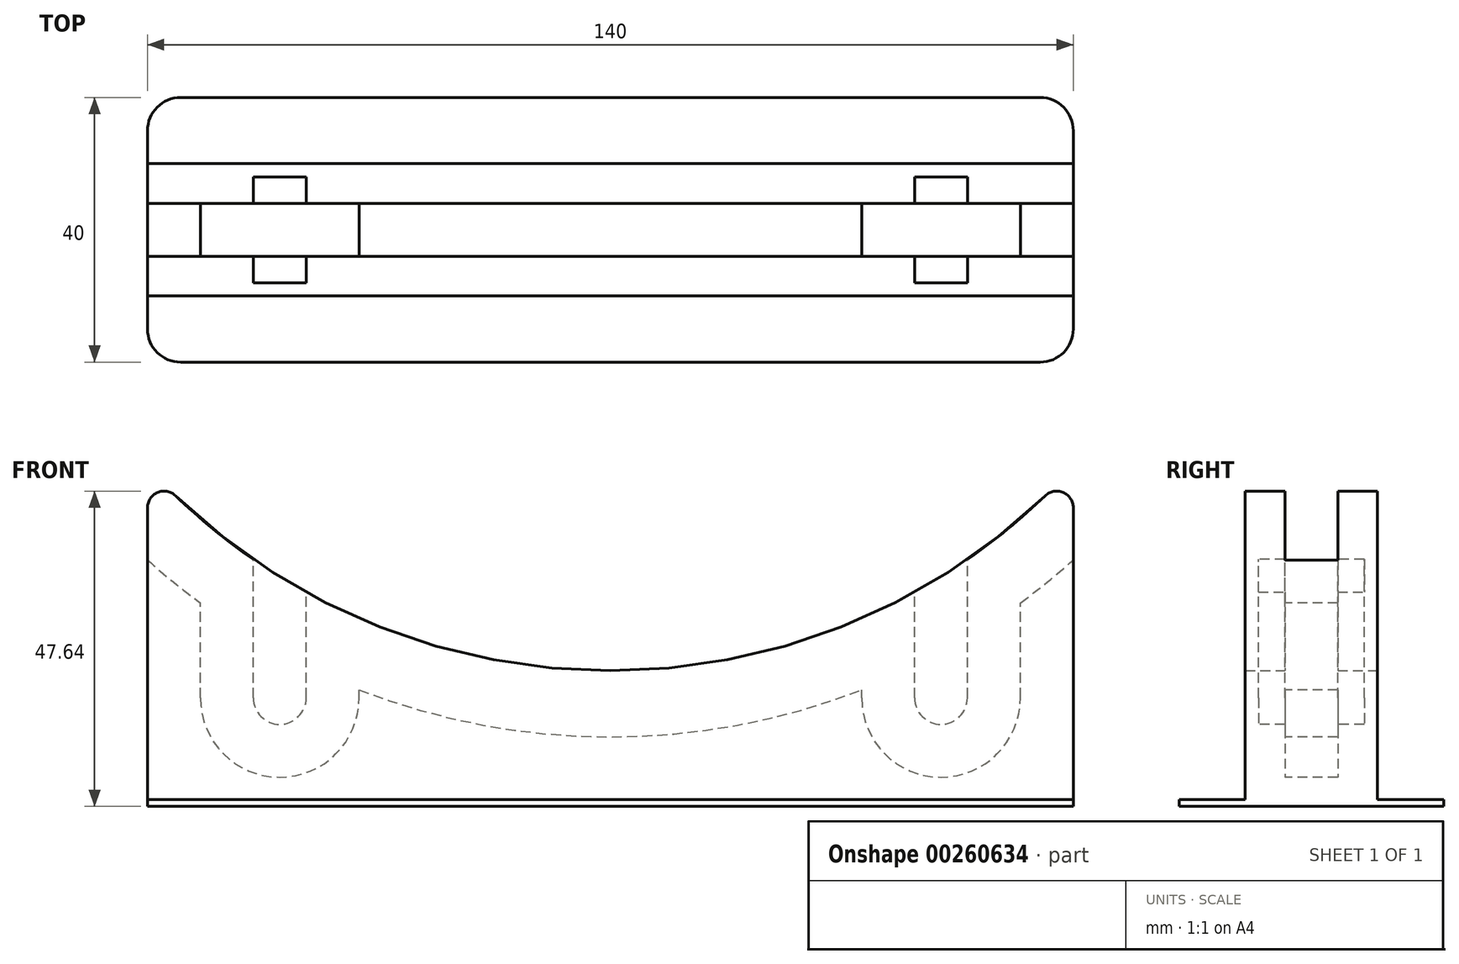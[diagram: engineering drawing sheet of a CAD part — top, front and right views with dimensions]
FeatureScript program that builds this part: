
annotation { "Feature Type Name" : "Feature", "Feature Type Description" : "" }
export const myFeature = defineFeature(function(context is Context, id is Id, definition is map)
    precondition{}
    {
        {
            var Q0;
            Q0=qCreatedBy(makeId("Front.planeOp"),FACE);
            var sketch = newSketch(context, id + "F0", { "sketchPlane" : qUnion([Q0])});
            skCircle(sketch, "E0", {"center": v(0, 115) * mm, "radius": 100 * mm, "construction": true});
            skLineSegment(sketch, "E1.top", {"start": v(-70, 0) * mm, "end": v(70, 0) * mm});
            skLineSegment(sketch, "E1.left", {"start": v(-70, 50.77) * mm, "end": v(-70, 0) * mm});
            skLineSegment(sketch, "E1.right", {"start": v(70, 50.77) * mm, "end": v(70, 0) * mm});
            skPoint(sketch, "E1.middle", {"position": v(0, 25.39) * mm});
            skArc(sketch, "E2", {"start": v(-70, 50.77) * mm, "mid": v(0, 20) * mm, "end": v(70, 50.77) * mm});
            skCircle(sketch, "E3", {"center": v(-50, 15.9) * mm, "radius": 11 * mm, "construction": true});
            skSolve(sketch);
        }
        {
            var Q0;
            Q0=makeQuery(id+"F0.imprint","IMPRINT",FACE,{"disambiguationData":[TD([[makeQuery(id+"F0.imprint","IMPRINT",EDGE,{"derivedFrom":sQuery(id+"F0.wireOp",EDGE,"E1.top")}),1.0]])]});
            extrude(context, id + "F1", {"entities" : qUnion([Q0]), "endBound" : BoundingType.SYMMETRIC, "depth" : 20 * mm, "hasSecondDirection" : true, "secondDirectionOppositeDirection" : true, "secondDirectionDepth" : 7.5 * mm});
        }
        {
            var Q0;
            Q0=qCreatedBy(makeId("Front.planeOp"),FACE);
            var sketch = newSketch(context, id + "F2", { "sketchPlane" : qUnion([Q0])});
            skCircle(sketch, "E4", {"center": v(0, 115) * mm, "radius": 100 * mm, "construction": true});
            skCircle(sketch, "E5", {"center": v(0, 115) * mm, "radius": 105 * mm});
            skSolve(sketch);
        }
        {
            var Q0;
            Q0=makeQuery(id+"F2.imprint","IMPRINT",FACE,{"disambiguationData":[TD([[makeQuery(id+"F2.imprint","IMPRINT",EDGE,{"derivedFrom":sQuery(id+"F2.wireOp",EDGE,"E5")}),1.0]])]});
            extrude(context, id + "F3", {"entities" : qUnion([Q0]), "operationType" : NewBodyOperationType.REMOVE, "oppositeDirection" : true, "depth" : 4 * mm, "hasSecondDirection" : true, "secondDirectionOppositeDirection" : false, "secondDirectionDepth" : 4 * mm});
        }
        {
            var Q0;
            {var subQ0=sQuery(id+"F0.wireOp",EDGE,"E2");var subQ1=sQuery(id+"F0.wireOp",EDGE,"E1.left");Q0=makeQuery(id+"F3.boolean.opBoolean","SPLIT",EDGE,{"disambiguationData":[TD([makeQuery(id+"F3.opExtrude","CAP_FACE",FACE,{"disambiguationData":[OSD([sQuery(id+"F2.wireOp",EDGE,"E5")])],"isStart":false})])],"derivedFrom":makeQuery(id+"F1.opExtrude","SWEPT_EDGE",EDGE,{"disambiguationData":[OSD([subQ1,subQ0])]})});}
            var Q1;
            {var subQ0=sQuery(id+"F0.wireOp",EDGE,"E2");var subQ1=sQuery(id+"F0.wireOp",EDGE,"E1.left");Q1=makeQuery(id+"F3.boolean.opBoolean","SPLIT",EDGE,{"disambiguationData":[TD([makeQuery(id+"F3.opExtrude","CAP_FACE",FACE,{"disambiguationData":[OSD([sQuery(id+"F2.wireOp",EDGE,"E5")])],"isStart":true})])],"derivedFrom":makeQuery(id+"F1.opExtrude","SWEPT_EDGE",EDGE,{"disambiguationData":[OSD([subQ1,subQ0])]})});}
            var Q2;
            {var subQ0=sQuery(id+"F0.wireOp",EDGE,"E2");var subQ1=sQuery(id+"F0.wireOp",EDGE,"E1.right");Q2=makeQuery(id+"F3.boolean.opBoolean","SPLIT",EDGE,{"disambiguationData":[TD([makeQuery(id+"F3.opExtrude","CAP_FACE",FACE,{"disambiguationData":[OSD([sQuery(id+"F2.wireOp",EDGE,"E5")])],"isStart":false})])],"derivedFrom":makeQuery(id+"F1.opExtrude","SWEPT_EDGE",EDGE,{"disambiguationData":[OSD([subQ1,subQ0])]})});}
            var Q3;
            {var subQ0=sQuery(id+"F0.wireOp",EDGE,"E2");var subQ1=sQuery(id+"F0.wireOp",EDGE,"E1.right");Q3=makeQuery(id+"F3.boolean.opBoolean","SPLIT",EDGE,{"disambiguationData":[TD([makeQuery(id+"F3.opExtrude","CAP_FACE",FACE,{"disambiguationData":[OSD([sQuery(id+"F2.wireOp",EDGE,"E5")])],"isStart":true})])],"derivedFrom":makeQuery(id+"F1.opExtrude","SWEPT_EDGE",EDGE,{"disambiguationData":[OSD([subQ1,subQ0])]})});}
            fillet(context, id + "F4", {"entities" : qUnion([Q0, Q1, Q2, Q3]), "radius" : 2.5 * mm, "tangentPropagation" : true, "allowEdgeOverflow" : false});
        }
        {
            var Q0;
            Q0=qCreatedBy(makeId("Front.planeOp"),FACE);
            var sketch = newSketch(context, id + "F5", { "sketchPlane" : qUnion([Q0])});
            skArc(sketch, "E6", {"start": v(-62, 15.9) * mm, "mid": v(-50, 3.9) * mm, "end": v(-38, 15.9) * mm});
            skCircle(sketch, "E7", {"center": v(0, 115) * mm, "radius": 100 * mm, "construction": true});
            skCircle(sketch, "E8", {"center": v(-50, 15.9) * mm, "radius": 11 * mm, "construction": true});
            skLineSegment(sketch, "E9.bottom", {"start": v(-62, 15.9) * mm, "end": v(-61, 15.9) * mm});
            skLineSegment(sketch, "E9.top", {"start": v(-62, 43.02) * mm, "end": v(-38, 43.02) * mm});
            skLineSegment(sketch, "E9.left", {"start": v(-62, 15.9) * mm, "end": v(-62, 43.02) * mm});
            skLineSegment(sketch, "E9.right", {"start": v(-38, 15.9) * mm, "end": v(-38, 43.02) * mm});
            skPoint(sketch, "E9.middle", {"position": v(-50, 29.46) * mm});
            skLineSegment(sketch, "E10.trimOffspring", {"start": v(-39, 15.9) * mm, "end": v(-38, 15.9) * mm});
            skLineSegment(sketch, "E11.MirrorCS", {"start": v(39, 15.9) * mm, "end": v(38, 15.9) * mm});
            skLineSegment(sketch, "E12.MirrorCS", {"start": v(62, 15.9) * mm, "end": v(61, 15.9) * mm});
            skArc(sketch, "E13.MirrorCS", {"start": v(62, 15.9) * mm, "mid": v(50, 3.9) * mm, "end": v(38, 15.9) * mm});
            skPoint(sketch, "E14.MirrorP", {"position": v(50, 29.46) * mm});
            skLineSegment(sketch, "E15.MirrorCS", {"start": v(38, 15.9) * mm, "end": v(38, 43.02) * mm});
            skLineSegment(sketch, "E16.MirrorCS", {"start": v(62, 43.02) * mm, "end": v(38, 43.02) * mm});
            skLineSegment(sketch, "E17.MirrorCS", {"start": v(62, 15.9) * mm, "end": v(62, 43.02) * mm});
            skCircle(sketch, "E18.MirrorC", {"center": v(50, 15.9) * mm, "radius": 11 * mm, "construction": true});
            skSolve(sketch);
        }
        {
            var Q0;
            Q0 = qSketchRegion(id + "F5", true);
            extrude(context, id + "F6", {"entities" : qUnion([Q0]), "operationType" : NewBodyOperationType.REMOVE, "endBound" : BoundingType.SYMMETRIC, "oppositeDirection" : true, "depth" : 8 * mm});
        }
        {
            var Q0;
            Q0=makeQuery(id+"F1.opExtrude","CAP_FACE",FACE,{"disambiguationData":[OSD([sQuery(id+"F0.wireOp",EDGE,"E1.top"),sQuery(id+"F0.wireOp",EDGE,"E1.left"),sQuery(id+"F0.wireOp",EDGE,"E1.right"),sQuery(id+"F0.wireOp",EDGE,"E2")])],"isStart":false});
            var sketch = newSketch(context, id + "F7", { "sketchPlane" : qUnion([Q0])});
            skArc(sketch, "E19", {"start": v(-54, 15.9) * mm, "mid": v(-50, 11.9) * mm, "end": v(-46, 15.9) * mm});
            skPoint(sketch, "E20.middle", {"position": v(-50, 26.4) * mm});
            skLineSegment(sketch, "E21", {"start": v(-54, 15.9) * mm, "end": v(-54, 36.84) * mm});
            skLineSegment(sketch, "E22", {"start": v(-54, 36.84) * mm, "end": v(-46, 36.84) * mm});
            skLineSegment(sketch, "E23", {"start": v(-46, 15.9) * mm, "end": v(-46, 36.84) * mm});
            skLineSegment(sketch, "E24.MirrorCS", {"start": v(54, 15.9) * mm, "end": v(54, 36.84) * mm});
            skLineSegment(sketch, "E25.MirrorCS", {"start": v(46, 15.9) * mm, "end": v(46, 36.84) * mm});
            skLineSegment(sketch, "E26.MirrorCS", {"start": v(54, 36.84) * mm, "end": v(46, 36.84) * mm});
            skPoint(sketch, "E27.MirrorP", {"position": v(50, 26.4) * mm});
            skArc(sketch, "E28.MirrorCS", {"start": v(54, 15.9) * mm, "mid": v(50, 11.9) * mm, "end": v(46, 15.9) * mm});
            skSolve(sketch);
        }
        {
            var Q0;
            Q0 = qSketchRegion(id + "F7", true);
            extrude(context, id + "F8", {"entities" : qUnion([Q0]), "operationType" : NewBodyOperationType.REMOVE, "oppositeDirection" : true, "depth" : 18 * mm, "hasSecondDirection" : true, "secondDirectionOppositeDirection" : true, "secondDirectionDepth" : 2 * mm});
        }
        {
            var Q0;
            Q0=qCreatedBy(makeId("Top.planeOp"),FACE);
            var sketch = newSketch(context, id + "F9", { "sketchPlane" : qUnion([Q0])});
            skLineSegment(sketch, "E29.bottom", {"start": v(-70, 20) * mm, "end": v(70, 20) * mm});
            skLineSegment(sketch, "E29.top", {"start": v(-70, -20) * mm, "end": v(70, -20) * mm});
            skLineSegment(sketch, "E29.left", {"start": v(-70, 20) * mm, "end": v(-70, -20) * mm});
            skLineSegment(sketch, "E29.right", {"start": v(70, 20) * mm, "end": v(70, -20) * mm});
            skPoint(sketch, "E29.middle", {"position": v(0, 0) * mm});
            skSolve(sketch);
        }
        {
            var Q0;
            Q0=makeQuery(id+"F9.imprint","IMPRINT",FACE,{"disambiguationData":[TD([[makeQuery(id+"F9.imprint","IMPRINT",EDGE,{"derivedFrom":sQuery(id+"F9.wireOp",EDGE,"E29.bottom")}),-1.0]])]});
            extrude(context, id + "F10", {"entities" : qUnion([Q0]), "operationType" : NewBodyOperationType.ADD, "endBound" : BoundingType.SYMMETRIC, "depth" : 1 * mm});
        }
        {
            var Q0;
            Q0=makeQuery(id+"F10.opExtrude","SWEPT_EDGE",EDGE,{"disambiguationData":[OSD([sQuery(id+"F9.wireOp",EDGE,"E29.top"),sQuery(id+"F9.wireOp",EDGE,"E29.left")])]});
            var Q1;
            Q1=makeQuery(id+"F10.opExtrude","SWEPT_EDGE",EDGE,{"disambiguationData":[OSD([sQuery(id+"F9.wireOp",EDGE,"E29.top"),sQuery(id+"F9.wireOp",EDGE,"E29.right")])]});
            var Q2;
            Q2=makeQuery(id+"F10.opExtrude","SWEPT_EDGE",EDGE,{"disambiguationData":[OSD([sQuery(id+"F9.wireOp",EDGE,"E29.bottom"),sQuery(id+"F9.wireOp",EDGE,"E29.right")])]});
            var Q3;
            Q3=makeQuery(id+"F10.opExtrude","SWEPT_EDGE",EDGE,{"disambiguationData":[OSD([sQuery(id+"F9.wireOp",EDGE,"E29.bottom"),sQuery(id+"F9.wireOp",EDGE,"E29.left")])]});
            fillet(context, id + "F11", {"entities" : qUnion([Q0, Q1, Q2, Q3]), "radius" : 5 * mm, "tangentPropagation" : true, "allowEdgeOverflow" : false});
        }
    });
